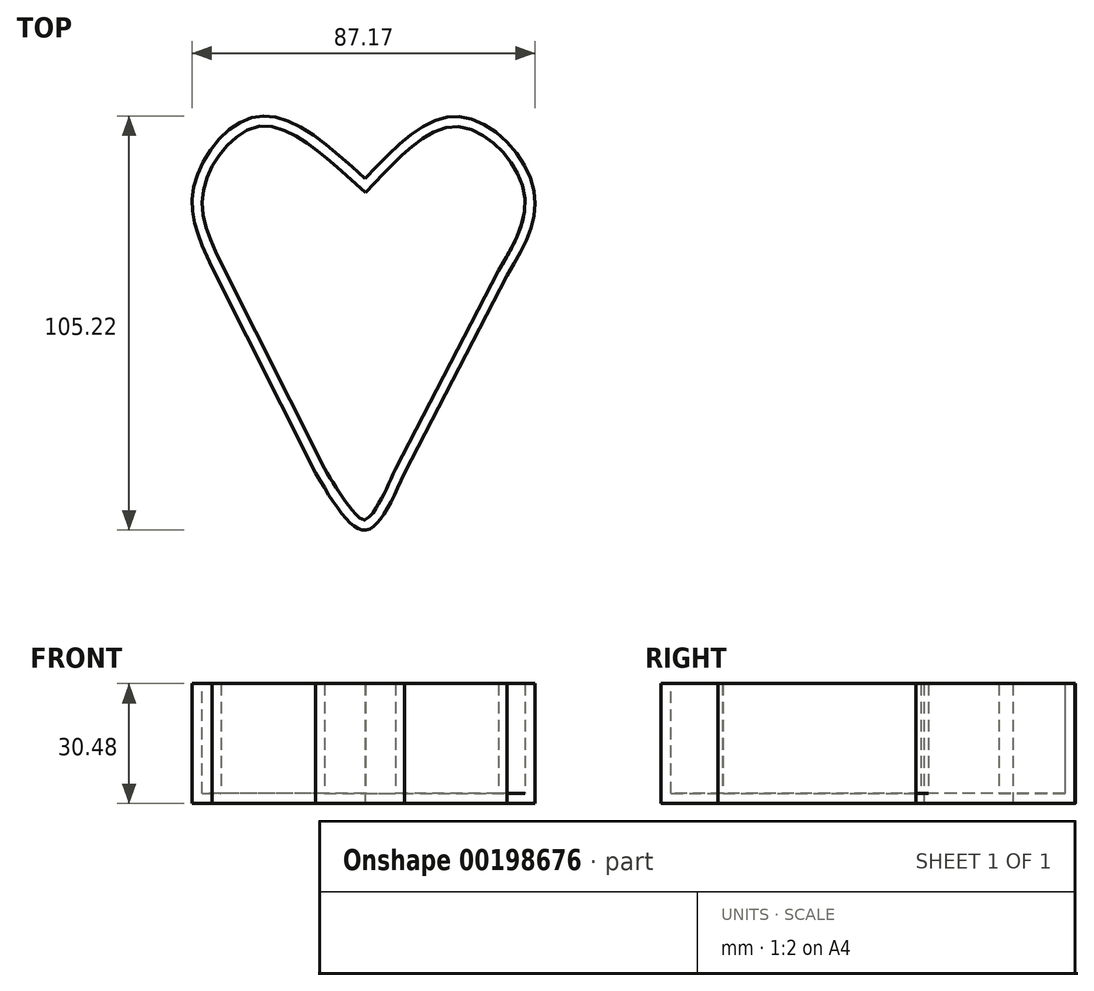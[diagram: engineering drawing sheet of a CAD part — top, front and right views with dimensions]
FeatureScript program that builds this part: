
annotation { "Feature Type Name" : "Feature", "Feature Type Description" : "" }
export const myFeature = defineFeature(function(context is Context, id is Id, definition is map)
    precondition{}
    {
        {
            var Q0;
            Q0=qCreatedBy(makeId("Top.planeOp"),FACE);
            var sketch = newSketch(context, id + "F0", { "sketchPlane" : qUnion([Q0])});
            skLineSegment(sketch, "E0", {"start": v(-12.6, -40.04) * mm, "end": v(-38.85, 12.2) * mm});
            skFitSpline(sketch, "E1", {"points": [v(0, 34.79) * mm, v(-27.57, 50.54) * mm, v(-43.58, 32.42) * mm, v(-38.85, 12.2) * mm], "startDerivative": vector(-76.15, 69.22) * mm, "endDerivative": vector(30.8, -64.1) * mm});
            skFitSpline(sketch, "E2", {"points": [v(0, 34.79) * mm, v(24.15, 50.54) * mm, v(42.78, 32.42) * mm, v(36.1, 10.18) * mm], "startDerivative": vector(66.72, 70.75) * mm, "endDerivative": vector(-40.43, -67.81) * mm});
            skLineSegment(sketch, "E3", {"start": v(36.1, 10.18) * mm, "end": v(9.98, -40.04) * mm});
            skFitSpline(sketch, "E4", {"points": [v(-12.6, -40.04) * mm, v(0, -54.51) * mm, v(9.98, -40.04) * mm], "startDerivative": vector(25.75, -43.13) * mm, "endDerivative": vector(19.36, 43.77) * mm});
            skSolve(sketch);
        }
        {
            var Q0;
            {var subQ0=sQuery(id+"F0.wireOp",EDGE,"E0");Q0=makeQuery(id+"F0.imprint","IMPRINT",FACE,{"disambiguationData":[TD([[makeQuery(id+"F0.imprint","IMPRINT",EDGE,{"derivedFrom":subQ0}),-1.0]])]});}
            extrude(context, id + "F1", {"entities" : qUnion([Q0]), "depth" : 30.48 * mm});
        }
        {
            var Q0;
            Q0=makeQuery(id+"F1.opExtrude","CAP_FACE",FACE,{"disambiguationData":[OSD([sQuery(id+"F0.wireOp",EDGE,"E0"),sQuery(id+"F0.wireOp",EDGE,"E1"),sQuery(id+"F0.wireOp",EDGE,"E2"),sQuery(id+"F0.wireOp",EDGE,"E3"),sQuery(id+"F0.wireOp",EDGE,"E4")])],"isStart":false});
            shell(context, id + "F2", {"entities" : qUnion([Q0]), "thickness" : 2.54 * mm});
        }
    });
